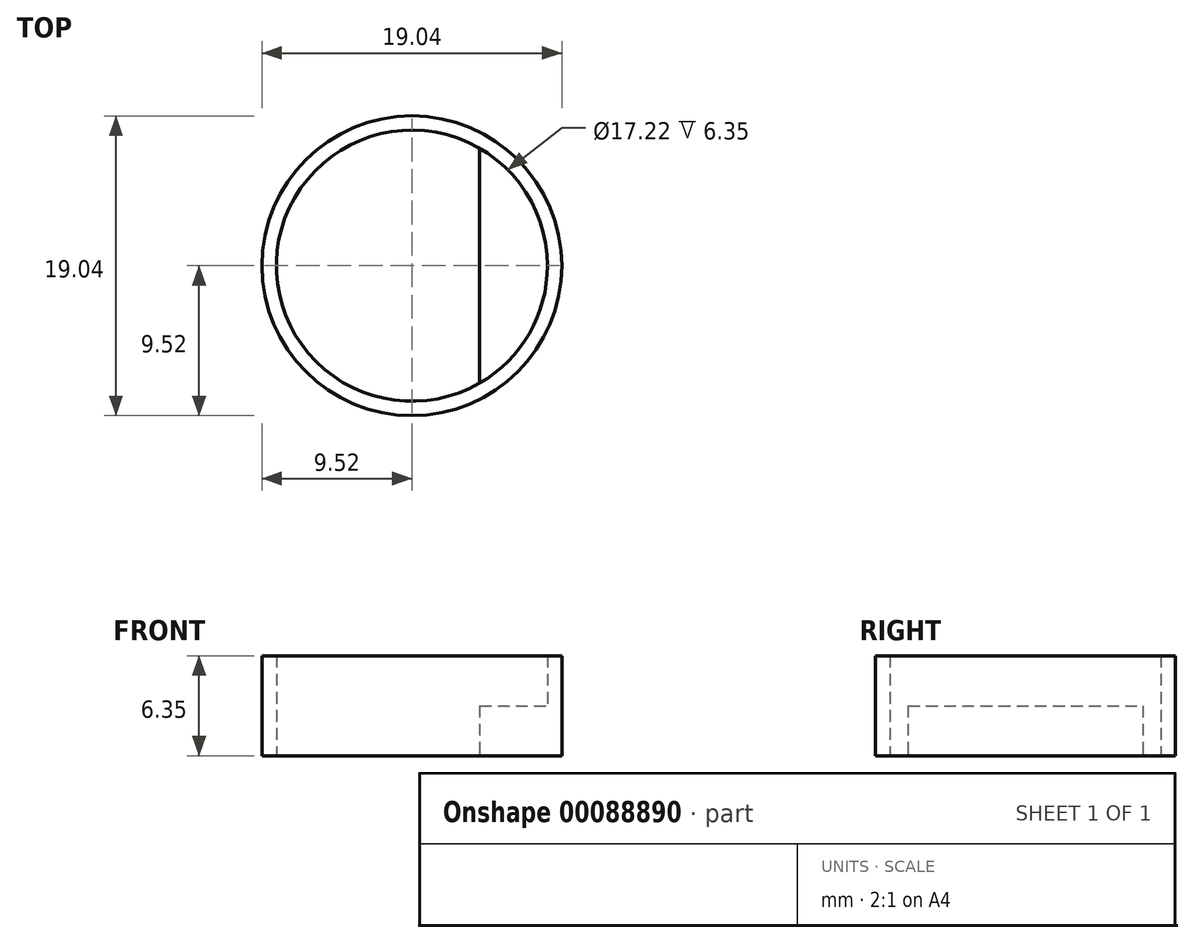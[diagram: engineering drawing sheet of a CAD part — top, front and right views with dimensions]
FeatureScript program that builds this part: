
annotation { "Feature Type Name" : "Feature", "Feature Type Description" : "" }
export const myFeature = defineFeature(function(context is Context, id is Id, definition is map)
    precondition{}
    {
        {
            var Q0;
            Q0=qCreatedBy(makeId("Top.planeOp"),FACE);
            var sketch = newSketch(context, id + "F0", { "sketchPlane" : qUnion([Q0])});
            skCircle(sketch, "E0", {"center": v(0, 0) * mm, "radius": 8.61 * mm});
            skCircle(sketch, "E1", {"center": v(0, 0) * mm, "radius": 9.52 * mm});
            skLineSegment(sketch, "E2", {"start": v(4.3, 0) * mm, "end": v(4.3, 7.46) * mm});
            skLineSegment(sketch, "E3", {"start": v(4.3, 7.46) * mm, "end": v(4.3, -7.46) * mm});
            skSolve(sketch);
        }
        {
            var Q0;
            {var subQ0=sQuery(id+"F0.wireOp",EDGE,"E3");var subQ4=makeQuery(id+"F0.imprint","IMPRINT",VERTEX,{"derivedFrom":subQ0});Q0=makeQuery(id+"F0.imprint","IMPRINT",FACE,{"disambiguationData":[TD([[makeQuery(id+"F0.imprint","IMPRINT",EDGE,{"disambiguationData":[TD([[subQ4,1.0]])],"derivedFrom":subQ0}),1.0]])]});}
            extrude(context, id + "F1", {"entities" : qUnion([Q0]), "depth" : 3.17 * mm});
        }
        {
            var Q0;
            Q0=makeQuery(id+"F0.imprint","IMPRINT",FACE,{"disambiguationData":[TD([[makeQuery(id+"F0.imprint","IMPRINT",EDGE,{"derivedFrom":sQuery(id+"F0.wireOp",EDGE,"E1")}),1.0]])]});
            extrude(context, id + "F2", {"entities" : qUnion([Q0]), "operationType" : NewBodyOperationType.ADD, "depth" : 6.35 * mm});
        }
    });
